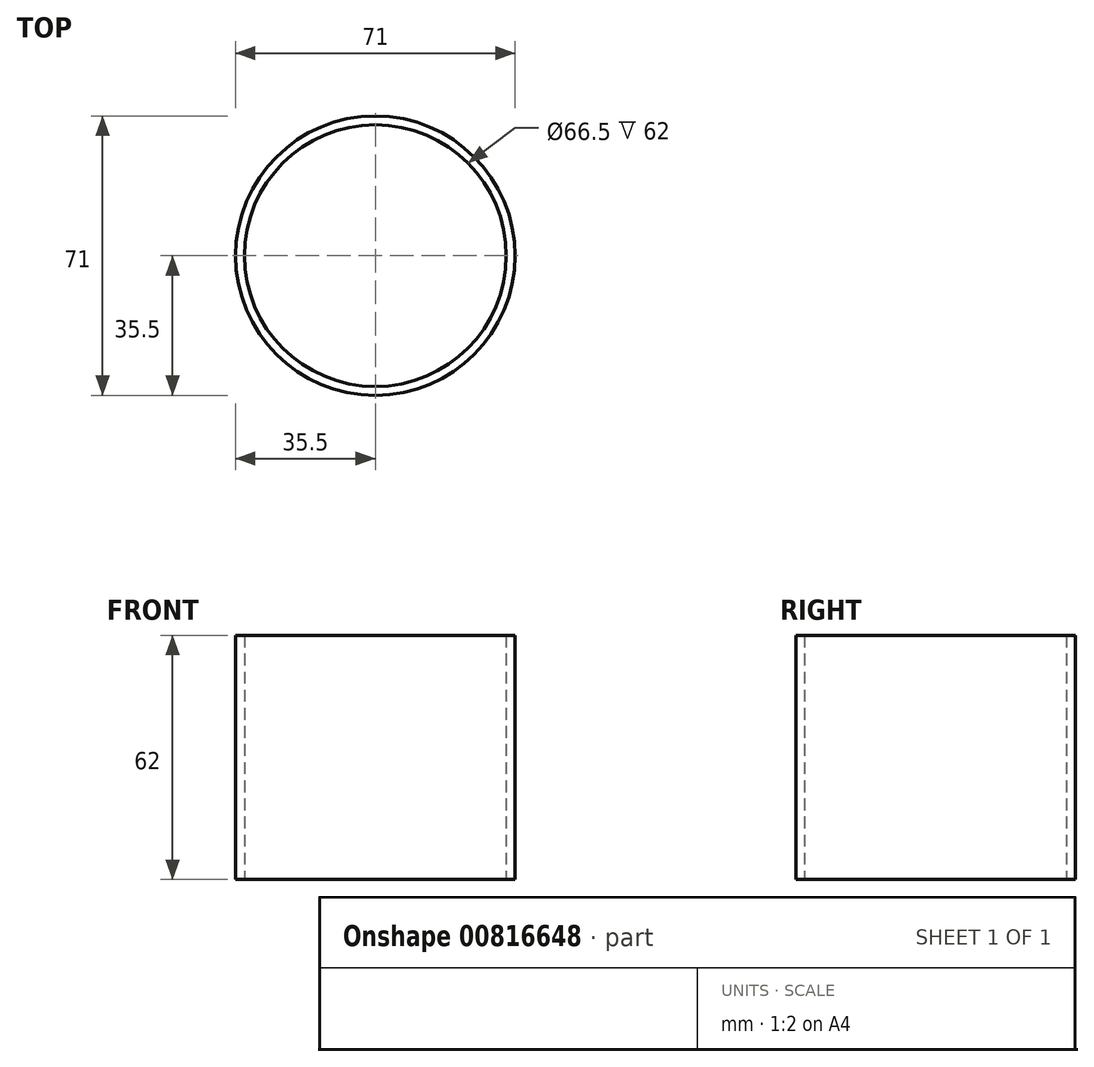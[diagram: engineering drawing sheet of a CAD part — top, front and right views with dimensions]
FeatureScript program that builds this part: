
annotation { "Feature Type Name" : "Feature", "Feature Type Description" : "" }
export const myFeature = defineFeature(function(context is Context, id is Id, definition is map)
    precondition{}
    {
        {
            var Q0;
            Q0=qCreatedBy(makeId("Top.planeOp"),FACE);
            var sketch = newSketch(context, id + "F0", { "sketchPlane" : qUnion([Q0])});
            skCircle(sketch, "E0", {"center": v(0, 0) * mm, "radius": 33.25 * mm});
            skCircle(sketch, "E1", {"center": v(0, 0) * mm, "radius": 35.5 * mm});
            skSolve(sketch);
        }
        {
            var Q0;
            Q0=makeQuery(id+"F0.imprint","IMPRINT",FACE,{"disambiguationData":[TD([[makeQuery(id+"F0.imprint","IMPRINT",EDGE,{"derivedFrom":sQuery(id+"F0.wireOp",EDGE,"E0")}),-1.0]])]});
            extrude(context, id + "F1", {"entities" : qUnion([Q0]), "depth" : 62 * mm, "offsetDistance" : 25 * mm});
        }
    });
